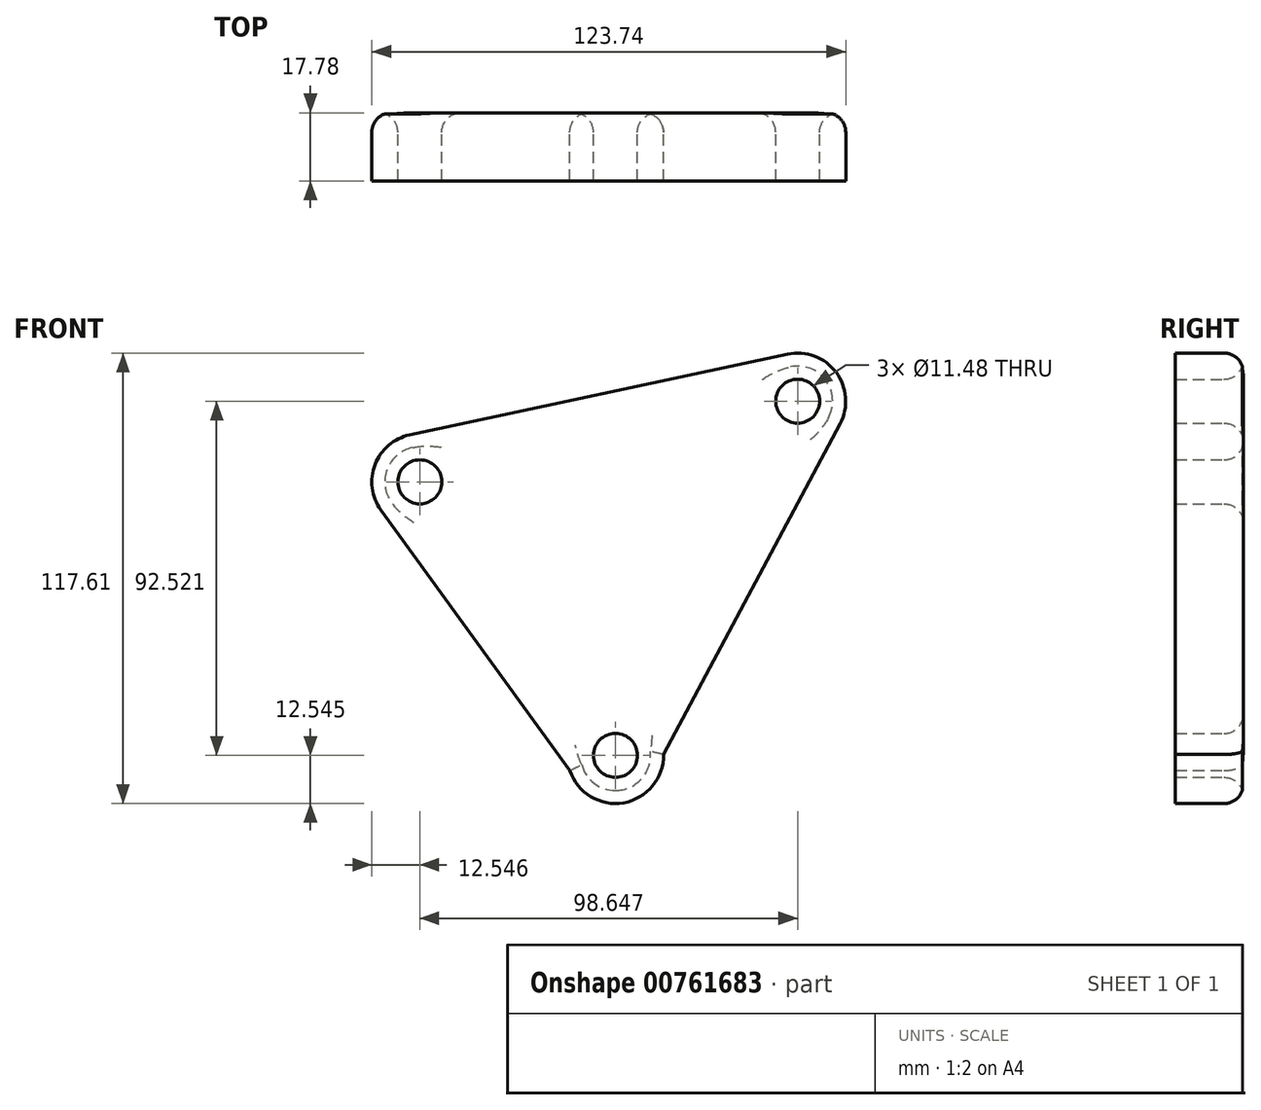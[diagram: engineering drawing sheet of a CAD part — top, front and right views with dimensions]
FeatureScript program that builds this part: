
annotation { "Feature Type Name" : "Feature", "Feature Type Description" : "" }
export const myFeature = defineFeature(function(context is Context, id is Id, definition is map)
    precondition{}
    {
        {
            var Q0;
            Q0=qCreatedBy(makeId("Front.planeOp"),FACE);
            var sketch = newSketch(context, id + "F0", { "sketchPlane" : qUnion([Q0])});
            skCircle(sketch, "E0", {"center": v(-53.37, 35.2) * mm, "radius": 5.74 * mm});
            skCircle(sketch, "E1", {"center": v(45.27, 56.28) * mm, "radius": 5.74 * mm});
            skCircle(sketch, "E2", {"center": v(-2.3, -36.25) * mm, "radius": 5.74 * mm});
            skCircle(sketch, "E3", {"center": v(-53.37, 35.2) * mm, "radius": 12.55 * mm});
            skCircle(sketch, "E4", {"center": v(45.27, 56.28) * mm, "radius": 12.55 * mm});
            skCircle(sketch, "E5", {"center": v(-2.3, -36.25) * mm, "radius": 12.55 * mm});
            skLineSegment(sketch, "E6", {"start": v(-14.2, -40.2) * mm, "end": v(-63.53, 27.85) * mm});
            skLineSegment(sketch, "E7", {"start": v(10.25, -35.99) * mm, "end": v(56.34, 50.37) * mm});
            skLineSegment(sketch, "E8", {"start": v(42.65, 68.55) * mm, "end": v(-56, 47.48) * mm});
            skArc(sketch, "E9", {"start": v(-56, 47.48) * mm, "mid": v(-4.9, 49.76) * mm, "end": v(42.65, 68.55) * mm});
            skArc(sketch, "E10", {"start": v(-14.2, -40.2) * mm, "mid": v(-29.04, 0.95) * mm, "end": v(-63.53, 27.85) * mm});
            skArc(sketch, "E11", {"start": v(56.34, 50.37) * mm, "mid": v(24.94, 11.65) * mm, "end": v(10.25, -35.99) * mm});
            skPoint(sketch, "E12", {"position": v(-63.53, 27.85) * mm});
            skSolve(sketch);
        }
        {
            var Q0;
            Q0=sQuery(id+"F0.wireOp",EDGE,"E3");
            var Q1;
            Q1=sQuery(id+"F0.wireOp",EDGE,"E4");
            var Q2;
            Q2=sQuery(id+"F0.wireOp",EDGE,"E5");
            extrude(context, id + "F1", {"bodyType" : ToolBodyType.SURFACE, "surfaceEntities" : qUnion([Q0, Q1, Q2]), "depth" : 17.78 * mm, "offsetDistance" : 25.4 * mm});
        }
        {
            var Q0;
            Q0 = qSketchRegion(id + "F0", true);
            extrude(context, id + "F2", {"entities" : qUnion([Q0]), "depth" : 17.78 * mm, "offsetDistance" : 25.4 * mm});
        }
        {
            var Q0;
            Q0=makeQuery(id+"F2.opExtrude","CAP_EDGE",EDGE,{"disambiguationData":[OSD([sQuery(id+"F0.wireOp",EDGE,"E6")])],"isStart":true});
            var Q1;
            Q1=makeQuery(id+"F2.opExtrude","CAP_FACE",FACE,{"disambiguationData":[OSD([sQuery(id+"F0.wireOp",EDGE,"E0"),sQuery(id+"F0.wireOp",EDGE,"E1"),sQuery(id+"F0.wireOp",EDGE,"E2"),sQuery(id+"F0.wireOp",EDGE,"E3"),sQuery(id+"F0.wireOp",EDGE,"E4"),sQuery(id+"F0.wireOp",EDGE,"E5"),sQuery(id+"F0.wireOp",EDGE,"E6"),sQuery(id+"F0.wireOp",EDGE,"E7"),sQuery(id+"F0.wireOp",EDGE,"E8")])],"isStart":true});
            fillet(context, id + "F3", {"entities" : qUnion([Q0, Q1]), "radius" : 5.08 * mm, "tangentPropagation" : true, "allowEdgeOverflow" : false});
        }
    });
